# Revit family: HVAC_Heaters_Superior-Radiant_Outdoor-Infrared-Heater-evenGLO-GA201M2
name_source: partatom
category: Mechanical Equipment
revit_build: Autodesk Revit 2018 (Build: 20190510_1515(x64)
units: mm (PartAtom-declared; Revit-internal decimal feet)

## family parameters
Always vertical = Yes
Classification = None
Cut with Voids When Loaded = No
OmniClass Number = 23.75.10.17.14.14
OmniClass Title = Fuel-Fired Radiant Heaters
Part Type = Normal
Room Calculation Point = No
Round Connector Dimension = Use Diameter
Shared = No
Work Plane-Based = No

## types (1)
- GA201M2
    Actual Heater Gas Flow = 0.2 GPM
    Assembly Code = D3020
    Description = The patented design and technology is far superior than the competition, beating out others in both looks and functionality.

58% more heat coverage
Comfort circle of 20-24 ft. diameter
Torch flame dispersed evenly to increase efficiency
316 marine grade stainless, 304 stainless, bronze, black and custom finishes available
Portable, fixed and hanging models available
    Edition number = 1
    Fuel Inlet Connector Description = 1/2“ NPT Gas Inlet
    Fuel Inlet Diameter = 0.5"
    Fuel Type = Liquid Propane
    Gas Manifold Pressure = 0.354 psi
    Keynote = 15800
    Manufacturer = Superior Radiant
    Maximum Fire Rate = 46000.00 Btu/h
    Maximum Inlet Pressure = 250.000 psi
    Model = evenGLO GA201M2
    Product Guid = 8817e2d6-bfa9-4198-bc79-d99a8c523388
    Product Material = Steel - Superior Radiant - Stainless Steel
    Product data url = https://www.bimobject.com
    URL = https://www.superiorradiant.com

## geometry (parser evidence)
native form markers: Sweep x8
no freeform markers — native parametric forms only
